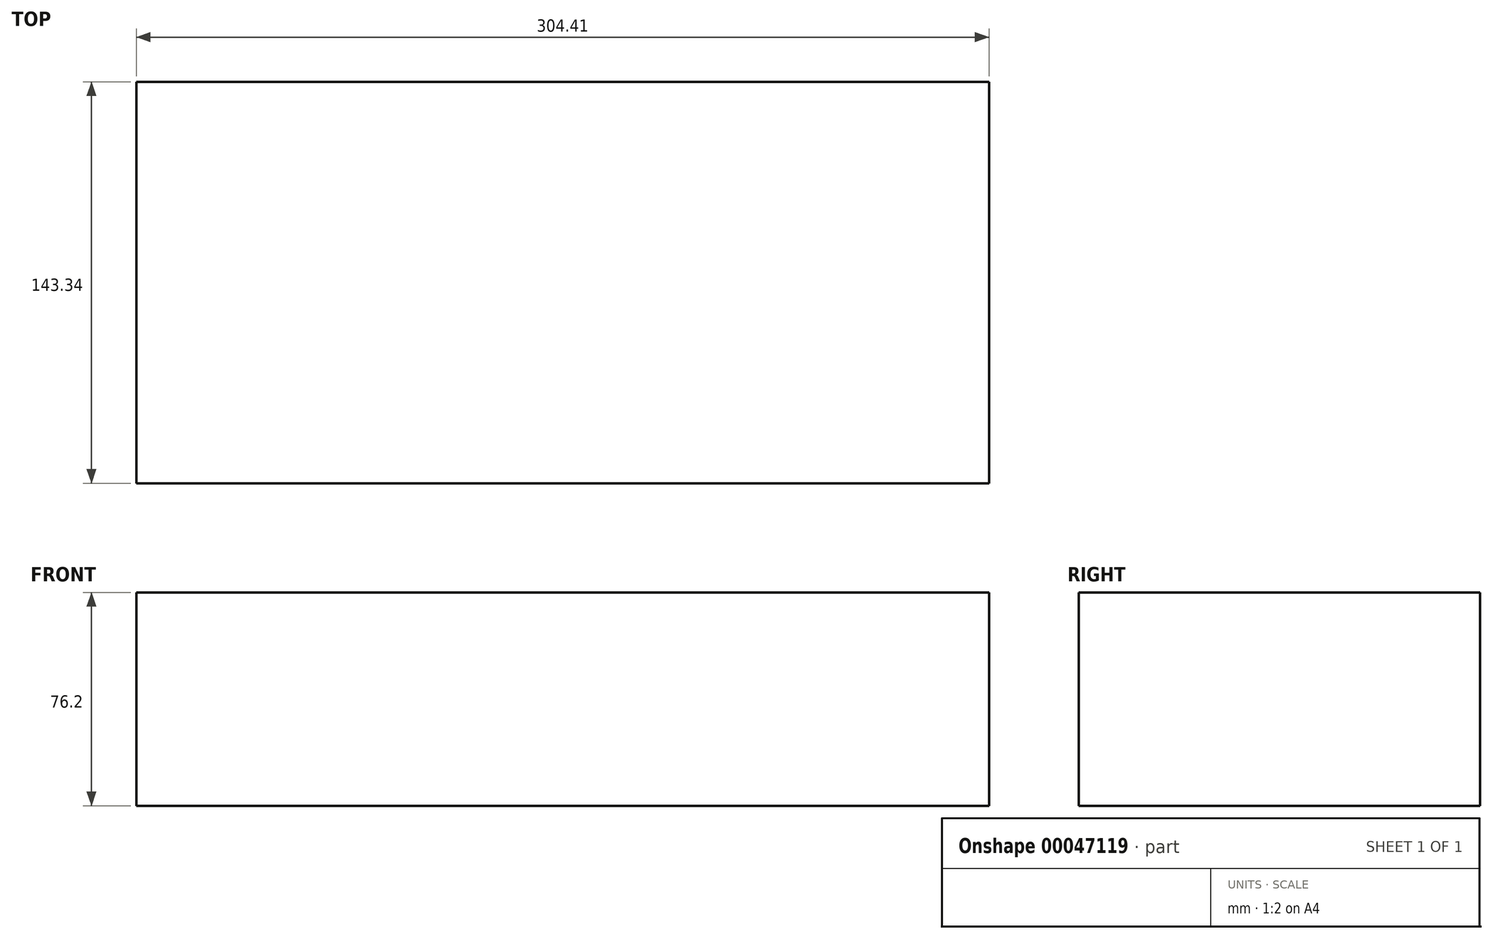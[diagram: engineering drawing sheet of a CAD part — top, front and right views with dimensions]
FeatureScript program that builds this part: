
annotation { "Feature Type Name" : "Feature", "Feature Type Description" : "" }
export const myFeature = defineFeature(function(context is Context, id is Id, definition is map)
    precondition{}
    {
        {
            var Q0;
            Q0=qCreatedBy(makeId("Top.planeOp"),FACE);
            var sketch = newSketch(context, id + "F0", { "sketchPlane" : qUnion([Q0])});
            skLineSegment(sketch, "E0.bottom", {"start": v(-234.9, 169.37) * mm, "end": v(69.5, 169.37) * mm});
            skLineSegment(sketch, "E0.top", {"start": v(-234.9, 26.03) * mm, "end": v(69.5, 26.03) * mm});
            skLineSegment(sketch, "E0.left", {"start": v(-234.9, 169.37) * mm, "end": v(-234.9, 26.03) * mm});
            skLineSegment(sketch, "E0.right", {"start": v(69.5, 169.37) * mm, "end": v(69.5, 26.03) * mm});
            skSolve(sketch);
        }
        {
            var Q0;
            Q0=makeQuery(id+"F0.imprint","IMPRINT",FACE,{"disambiguationData":[TD([[makeQuery(id+"F0.imprint","IMPRINT",EDGE,{"derivedFrom":sQuery(id+"F0.wireOp",EDGE,"E0.bottom")}),-1.0]])]});
            extrude(context, id + "F1", {"entities" : qUnion([Q0]), "depth" : 76.2 * mm});
        }
    });
